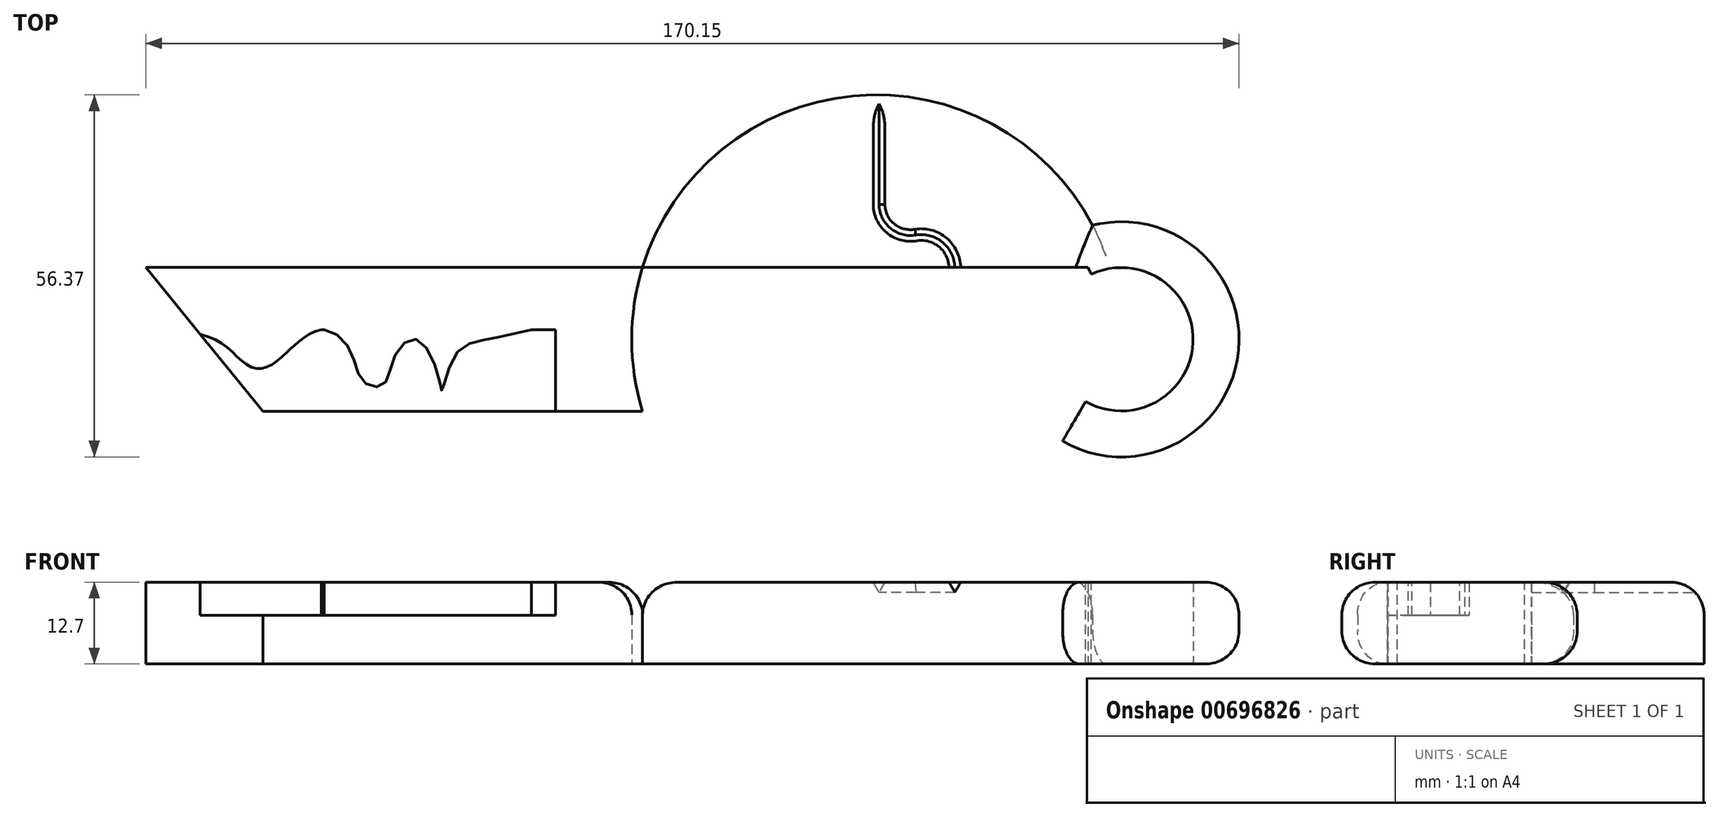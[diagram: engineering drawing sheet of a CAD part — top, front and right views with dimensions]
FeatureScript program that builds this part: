
annotation { "Feature Type Name" : "Feature", "Feature Type Description" : "" }
export const myFeature = defineFeature(function(context is Context, id is Id, definition is map)
    precondition{}
    {
        {
            var Q0;
            Q0=qCreatedBy(makeId("Top.planeOp"),FACE);
            var sketch = newSketch(context, id + "F0", { "sketchPlane" : qUnion([Q0])});
            skLineSegment(sketch, "E0", {"start": v(-76.55, 0) * mm, "end": v(76.12, 0) * mm});
            skLineSegment(sketch, "E1", {"start": v(0, 77.38) * mm, "end": v(0, -75.9) * mm});
            skLineSegment(sketch, "E2", {"start": v(0, 0) * mm, "end": v(76.12, 0) * mm});
            skLineSegment(sketch, "E3", {"start": v(38.06, 0) * mm, "end": v(38.06, 75.69) * mm});
            skCircle(sketch, "E4", {"center": v(38.06, 0) * mm, "radius": 38.06 * mm});
            skLineSegment(sketch, "E5.bottom", {"start": v(-75.64, 11.2) * mm, "end": v(74.43, 11.2) * mm});
            skLineSegment(sketch, "E5.top", {"start": v(-75.64, -11.2) * mm, "end": v(1.69, -11.2) * mm});
            skLineSegment(sketch, "E5.left", {"start": v(-75.64, 11.2) * mm, "end": v(-75.64, -11.2) * mm});
            skPoint(sketch, "E5.middle", {"position": v(0, 0) * mm});
            skSolve(sketch);
        }
        {
            var Q0;
            {var subQ0=sQuery(id+"F0.wireOp",EDGE,"E4");var subQ1=sQuery(id+"F0.wireOp",EDGE,"E3");var subQ2=makeQuery(id+"F0.imprint","INTERSECT",VERTEX,{"derivedFrom":[subQ1,subQ0]});Q0=makeQuery(id+"F0.imprint","IMPRINT",FACE,{"disambiguationData":[TD([[makeQuery(id+"F0.imprint","IMPRINT",EDGE,{"disambiguationData":[TD([[subQ2,1.0]])],"derivedFrom":subQ1}),1.0]])]});}
            var Q1;
            {var subQ0=sQuery(id+"F0.wireOp",EDGE,"E4");var subQ1=sQuery(id+"F0.wireOp",EDGE,"E3");var subQ2=makeQuery(id+"F0.imprint","INTERSECT",VERTEX,{"derivedFrom":[subQ1,subQ0]});Q1=makeQuery(id+"F0.imprint","IMPRINT",FACE,{"disambiguationData":[TD([[makeQuery(id+"F0.imprint","IMPRINT",EDGE,{"disambiguationData":[TD([[subQ2,1.0]])],"derivedFrom":subQ1}),-1.0]])]});}
            var Q2;
            {var subQ0=sQuery(id+"F0.wireOp",EDGE,"E4");var subQ1=sQuery(id+"F0.wireOp",EDGE,"E2");var subQ2=makeQuery(id+"F0.imprint","INTERSECT",VERTEX,{"derivedFrom":[subQ1,subQ0]});Q2=makeQuery(id+"F0.imprint","IMPRINT",FACE,{"disambiguationData":[TD([[makeQuery(id+"F0.imprint","IMPRINT",EDGE,{"disambiguationData":[TD([[subQ2,1.0]])],"derivedFrom":subQ1}),1.0]])]});}
            var Q3;
            {var subQ1=sQuery(id+"F0.wireOp",EDGE,"E2");var subQ3=sQuery(id+"F0.wireOp",EDGE,"E3");var subQ4=makeQuery(id+"F0.imprint","INTERSECT",VERTEX,{"derivedFrom":[subQ1,subQ3]});Q3=makeQuery(id+"F0.imprint","IMPRINT",FACE,{"disambiguationData":[TD([[makeQuery(id+"F0.imprint","IMPRINT",EDGE,{"disambiguationData":[TD([[subQ4,-1.0]])],"derivedFrom":subQ3}),1.0]])]});}
            var Q4;
            {var subQ0=sQuery(id+"F0.wireOp",EDGE,"E4");var subQ1=sQuery(id+"F0.wireOp",EDGE,"E2");var subQ4=makeQuery(id+"F0.imprint","INTERSECT",VERTEX,{"derivedFrom":[subQ1,subQ0]});Q4=makeQuery(id+"F0.imprint","IMPRINT",FACE,{"disambiguationData":[TD([[makeQuery(id+"F0.imprint","IMPRINT",EDGE,{"disambiguationData":[TD([[subQ4,1.0]])],"derivedFrom":subQ1}),-1.0]])]});}
            var Q5;
            {var subQ3=sQuery(id+"F0.wireOp",EDGE,"E5.left");var subQ5=sQuery(id+"F0.wireOp",EDGE,"E5.top");var subQ6=makeQuery(id+"F0.imprint","INTERSECT",VERTEX,{"derivedFrom":[subQ5,subQ3]});Q5=makeQuery(id+"F0.imprint","IMPRINT",FACE,{"disambiguationData":[TD([[makeQuery(id+"F0.imprint","IMPRINT",EDGE,{"disambiguationData":[TD([[subQ6,-1.0]])],"derivedFrom":subQ5}),1.0]])]});}
            var Q6;
            {var subQ3=sQuery(id+"F0.wireOp",EDGE,"E5.left");var subQ5=sQuery(id+"F0.wireOp",EDGE,"E5.bottom");var subQ7=makeQuery(id+"F0.imprint","INTERSECT",VERTEX,{"derivedFrom":[subQ5,subQ3]});Q6=makeQuery(id+"F0.imprint","IMPRINT",FACE,{"disambiguationData":[TD([[makeQuery(id+"F0.imprint","IMPRINT",EDGE,{"disambiguationData":[TD([[subQ7,-1.0]])],"derivedFrom":subQ5}),-1.0]])]});}
            var Q7;
            {var subQ1=sQuery(id+"F0.wireOp",EDGE,"E1");var subQ3=sQuery(id+"F0.wireOp",EDGE,"E5.bottom");var subQ4=makeQuery(id+"F0.imprint","INTERSECT",VERTEX,{"derivedFrom":[subQ1,subQ3]});Q7=makeQuery(id+"F0.imprint","IMPRINT",FACE,{"disambiguationData":[TD([[makeQuery(id+"F0.imprint","IMPRINT",EDGE,{"disambiguationData":[TD([[subQ4,-1.0]])],"derivedFrom":subQ3}),-1.0]])]});}
            var Q8;
            {var subQ0=sQuery(id+"F0.wireOp",EDGE,"E4");var subQ3=sQuery(id+"F0.wireOp",EDGE,"E5.top");var subQ5=makeQuery(id+"F0.imprint","INTERSECT",VERTEX,{"derivedFrom":[subQ0,subQ3]});Q8=makeQuery(id+"F0.imprint","IMPRINT",FACE,{"disambiguationData":[TD([[makeQuery(id+"F0.imprint","IMPRINT",EDGE,{"disambiguationData":[TD([[subQ5,1.0]])],"derivedFrom":subQ3}),1.0]])]});}
            extrude(context, id + "F1", {"entities" : qUnion([Q0, Q1, Q2, Q3, Q4, Q5, Q6, Q7, Q8]), "depth" : 12.7 * mm, "offsetDistance" : 25.4 * mm});
        }
        {
            var Q0;
            Q0=makeQuery(id+"F1.opExtrude","SWEPT_FACE",FACE,{"disambiguationData":[OSD([sQuery(id+"F0.wireOp",EDGE,"E5.top")])]});
            var sketch = newSketch(context, id + "F2", { "sketchPlane" : qUnion([Q0])});
            skPoint(sketch, "E6.oppositeSnap0", {"position": v(1.69, 6.35) * mm});
            skLineSegment(sketch, "E7.bottom", {"start": v(-75.64, 12.7) * mm, "end": v(-11.84, 12.7) * mm});
            skLineSegment(sketch, "E7.top", {"start": v(-75.64, 7.53) * mm, "end": v(-11.84, 7.53) * mm});
            skLineSegment(sketch, "E7.left", {"start": v(-75.64, 12.7) * mm, "end": v(-75.64, 7.53) * mm});
            skLineSegment(sketch, "E7.right", {"start": v(-11.84, 12.7) * mm, "end": v(-11.84, 7.53) * mm});
            skSolve(sketch);
        }
        {
            var Q0;
            Q0=qSketchRegion(id+"F2",true);
            extrude(context, id + "F3", {"entities" : qUnion([Q0]), "operationType" : NewBodyOperationType.REMOVE, "oppositeDirection" : true, "depth" : 12.7 * mm, "offsetDistance" : 25.4 * mm});
        }
        {
            var Q0;
            Q0=makeQuery(id+"F3.boolean.opBoolean","COPY",FACE,{"derivedFrom":makeQuery(id+"F3.opExtrude","SWEPT_FACE",FACE,{"disambiguationData":[OSD([sQuery(id+"F2.wireOp",EDGE,"E7.top")])]})});
            var sketch = newSketch(context, id + "F4", { "sketchPlane" : qUnion([Q0])});
            skPoint(sketch, "E8.8.internal.snap0", {"position": v(-43.74, 1.5) * mm});
            skFitSpline(sketch, "E8", {"points": [v(-71.4, 1.5) * mm, v(-64.86, 0) * mm, v(-61.37, -2.73) * mm, v(-58.75, -4.47) * mm, v(-56.14, -4.03) * mm, v(-53.52, -1.85) * mm, v(-51.34, 0) * mm, v(-47.85, 1.5) * mm, v(-43.74, -1.85) * mm, v(-41.75, -6.65) * mm, v(-38.7, -7.09) * mm, v(-36.95, -2.73) * mm, v(-33.46, 0) * mm, v(-29.98, -6.21) * mm, v(-29.54, -7.96) * mm, v(-27.36, -2.29) * mm, v(-22.56, 0) * mm, v(-15.59, 1.5) * mm], "startDerivative": vector(98.42, -12.85) * mm, "endDerivative": vector(95.91, 21.9) * mm});
            skLineSegment(sketch, "E9", {"start": v(-71.4, 1.5) * mm, "end": v(-15.59, 1.5) * mm});
            skSolve(sketch);
        }
        {
            var Q0;
            {var subQ0=sQuery(id+"F4.wireOp",EDGE,"E9");var subQ1=sQuery(id+"F4.wireOp",EDGE,"E8");var subQ3=makeQuery(id+"F4.imprint","INTERSECT",VERTEX,{"disambiguationData":[OD(0.0)],"derivedFrom":[subQ1,subQ0]});Q0=makeQuery(id+"F4.imprint","IMPRINT",FACE,{"disambiguationData":[TD([[makeQuery(id+"F4.imprint","IMPRINT",EDGE,{"disambiguationData":[TD([[subQ3,1.0]])],"derivedFrom":subQ1}),1.0]])]});}
            var Q1;
            {var subQ0=sQuery(id+"F4.wireOp",EDGE,"E9");var subQ1=sQuery(id+"F4.wireOp",EDGE,"E8");var subQ3=makeQuery(id+"F4.imprint","INTERSECT",VERTEX,{"disambiguationData":[OD(1.0)],"derivedFrom":[subQ1,subQ0]});Q1=makeQuery(id+"F4.imprint","IMPRINT",FACE,{"disambiguationData":[TD([[makeQuery(id+"F4.imprint","IMPRINT",EDGE,{"disambiguationData":[TD([[subQ3,-1.0]])],"derivedFrom":subQ1}),1.0]])]});}
            var Q2;
            Q2=makeQuery(id+"F1.opExtrude","CAP_FACE",FACE,{"disambiguationData":[OSD([sQuery(id+"F0.wireOp",EDGE,"E4"),sQuery(id+"F0.wireOp",EDGE,"E5.bottom"),sQuery(id+"F0.wireOp",EDGE,"E5.top"),sQuery(id+"F0.wireOp",EDGE,"E5.left")])],"isStart":false});
            extrude(context, id + "F5", {"entities" : qUnion([Q0, Q1]), "operationType" : NewBodyOperationType.ADD, "endBound" : BoundingType.UP_TO_SURFACE, "depth" : 25.4 * mm, "endBoundEntityFace" : qUnion([Q2]), "offsetDistance" : 25.4 * mm});
        }
        {
            var Q0;
            {var subQ0=sQuery(id+"F0.wireOp",EDGE,"E5.left");var subQ1=sQuery(id+"F0.wireOp",EDGE,"E5.top");var subQ2=sQuery(id+"F0.wireOp",EDGE,"E5.bottom");var subQ3=sQuery(id+"F0.wireOp",EDGE,"E4");Q0=makeQuery(id+"F5.boolean.opBoolean","MERGE",FACE,{"derivedFrom":[makeQuery(id+"F1.opExtrude","CAP_FACE",FACE,{"disambiguationData":[OSD([subQ3,subQ2,subQ1,subQ0])],"isStart":false}),makeQuery(id+"F5.opExtrude","CAP_FACE",FACE,{"disambiguationData":[OSD([subQ3,subQ2,subQ1,subQ0]),OD(0.0)],"isStart":false}),makeQuery(id+"F5.opExtrude","CAP_FACE",FACE,{"disambiguationData":[OSD([subQ3,subQ2,subQ1,subQ0]),OD(1.0)],"isStart":false})]});}
            var sketch = newSketch(context, id + "F6", { "sketchPlane" : qUnion([Q0])});
            skLineSegment(sketch, "E10", {"start": v(-54.4, -14.93) * mm, "end": v(-80.56, -12.75) * mm});
            skLineSegment(sketch, "E11", {"start": v(-80.56, -12.75) * mm, "end": v(-75.64, 11.2) * mm});
            skLineSegment(sketch, "E12", {"start": v(-75.64, 11.2) * mm, "end": v(-54.4, -14.93) * mm});
            skSolve(sketch);
        }
        {
            var Q0;
            Q0=qSketchRegion(id+"F6",true);
            extrude(context, id + "F7", {"entities" : qUnion([Q0]), "operationType" : NewBodyOperationType.REMOVE, "endBound" : BoundingType.THROUGH_ALL, "oppositeDirection" : true, "depth" : 25.4 * mm, "offsetDistance" : 25.4 * mm});
        }
        {
            var Q0;
            Q0=qCreatedBy(makeId("Right.planeOp"),FACE);
            cPlane(context, id + "F8", {"entities" : qUnion([Q0]), "cplaneType" : CPlaneType.OFFSET, "offset" : 76.2 * mm, "width" : 152.4 * mm, "height" : 152.4 * mm});
        }
        {
            var Q0;
            Q0=qCreatedBy(id+"F8.planeOp",FACE);
            var sketch = newSketch(context, id + "F9", { "sketchPlane" : qUnion([Q0])});
            skLineSegment(sketch, "E13", {"start": v(0, -5.67) * mm, "end": v(0, 19.48) * mm});
            skLineSegment(sketch, "E14.top", {"start": v(11.16, 0) * mm, "end": v(18.3, 0) * mm});
            skLineSegment(sketch, "E15", {"start": v(11.16, 0) * mm, "end": v(11.16, 12.7) * mm});
            skLineSegment(sketch, "E16", {"start": v(11.16, 12.7) * mm, "end": v(18.3, 12.7) * mm});
            skLineSegment(sketch, "E17", {"start": v(18.3, 12.7) * mm, "end": v(18.3, 0) * mm});
            skSolve(sketch);
        }
        {
            var Q0;
            Q0=makeQuery(id+"F9.imprint","IMPRINT",FACE,{"disambiguationData":[TD([[makeQuery(id+"F9.imprint","IMPRINT",EDGE,{"derivedFrom":sQuery(id+"F9.wireOp",EDGE,"E14.top")}),1.0]])]});
            var Q1;
            Q1=sQuery(id+"F9.wireOp",EDGE,"E13");
            revolve(context, id + "F10", {"operationType" : NewBodyOperationType.ADD, "entities" : qUnion([Q0]), "axis" : qUnion([Q1]), "revolveType" : RevolveType.TWO_DIRECTIONS, "angle" : 25 * degree, "angleBack" : 150 * degree});
        }
        {
            var Q0;
            Q0=qCreatedBy(makeId("Front.planeOp"),FACE);
            cPlane(context, id + "F11", {"entities" : qUnion([Q0]), "cplaneType" : CPlaneType.OFFSET, "offset" : 38.1 * mm, "width" : 152.4 * mm, "height" : 152.4 * mm});
        }
        {
            var Q0;
            {var subQ0=sQuery(id+"F0.wireOp",EDGE,"E5.left");var subQ1=sQuery(id+"F0.wireOp",EDGE,"E5.top");var subQ2=sQuery(id+"F0.wireOp",EDGE,"E5.bottom");var subQ3=sQuery(id+"F0.wireOp",EDGE,"E4");Q0=makeQuery(id+"F5.boolean.opBoolean","MERGE",FACE,{"derivedFrom":[makeQuery(id+"F1.opExtrude","CAP_FACE",FACE,{"disambiguationData":[OSD([subQ3,subQ2,subQ1,subQ0])],"isStart":false}),makeQuery(id+"F5.opExtrude","CAP_FACE",FACE,{"disambiguationData":[OSD([subQ3,subQ2,subQ1,subQ0]),OD(0.0)],"isStart":false}),makeQuery(id+"F5.opExtrude","CAP_FACE",FACE,{"disambiguationData":[OSD([subQ3,subQ2,subQ1,subQ0]),OD(1.0)],"isStart":false})]});}
            var sketch = newSketch(context, id + "F12", { "sketchPlane" : qUnion([Q0])});
            skLineSegment(sketch, "E18", {"start": v(38.5, -38.06) * mm, "end": v(38.5, -21.04) * mm});
            skArc(sketch, "E19", {"start": v(38.5, -21.04) * mm, "mid": v(40.22, -17.32) * mm, "end": v(44.17, -16.24) * mm});
            skArc(sketch, "E20", {"start": v(44.17, -16.24) * mm, "mid": v(48.62, -14.91) * mm, "end": v(50.28, -10.57) * mm});
            skLineSegment(sketch, "E21", {"start": v(50.28, -10.57) * mm, "end": v(50.28, 0) * mm});
            skLineSegment(sketch, "E22", {"start": v(0, 0) * mm, "end": v(43.3, 0) * mm});
            skLineSegment(sketch, "E23.MirrorCS", {"start": v(50.28, 10.57) * mm, "end": v(50.28, 0) * mm});
            skArc(sketch, "E24.MirrorCS", {"start": v(44.17, 16.24) * mm, "mid": v(48.62, 14.91) * mm, "end": v(50.28, 10.57) * mm});
            skArc(sketch, "E25.MirrorCS", {"start": v(38.5, 21.04) * mm, "mid": v(40.22, 17.32) * mm, "end": v(44.17, 16.24) * mm});
            skLineSegment(sketch, "E26.MirrorCS", {"start": v(38.5, 38.06) * mm, "end": v(38.5, 21.04) * mm});
            skSolve(sketch);
        }
        {
            var Q0;
            Q0=qCreatedBy(id+"F11.planeOp",FACE);
            var sketch = newSketch(context, id + "F13", { "sketchPlane" : qUnion([Q0])});
            skCircle(sketch, "E27.cCircle", {"center": v(38.5, 12.73) * mm, "radius": 1.6 * mm, "construction": true});
            skLineSegment(sketch, "E27.0", {"start": v(38.5, 11.14) * mm, "end": v(37.1, 13.53) * mm});
            skLineSegment(sketch, "E27.1", {"start": v(37.1, 13.53) * mm, "end": v(39.87, 13.53) * mm});
            skLineSegment(sketch, "E27.2", {"start": v(39.87, 13.53) * mm, "end": v(38.5, 11.14) * mm});
            skSolve(sketch);
        }
        {
            var Q0;
            Q0=makeQuery(id+"F13.imprint","IMPRINT",FACE,{"disambiguationData":[TD([[makeQuery(id+"F13.imprint","IMPRINT",EDGE,{"derivedFrom":sQuery(id+"F13.wireOp",EDGE,"E27.0")}),-1.0]])]});
            var Q1;
            Q1=sQuery(id+"F12.wireOp",EDGE,"E18");
            var Q2;
            Q2=sQuery(id+"F12.wireOp",EDGE,"E19");
            var Q3;
            Q3=sQuery(id+"F12.wireOp",EDGE,"E20");
            var Q4;
            Q4=sQuery(id+"F12.wireOp",EDGE,"E21");
            var Q5;
            Q5=sQuery(id+"F12.wireOp",EDGE,"E23.MirrorCS");
            var Q6;
            Q6=sQuery(id+"F12.wireOp",EDGE,"E24.MirrorCS");
            var Q7;
            Q7=sQuery(id+"F12.wireOp",EDGE,"E25.MirrorCS");
            var Q8;
            Q8=sQuery(id+"F12.wireOp",EDGE,"E26.MirrorCS");
            sweep(context, id + "F14", {"operationType" : NewBodyOperationType.REMOVE, "profiles" : qUnion([Q0]), "path" : qUnion([Q1, Q2, Q3, Q4, Q5, Q6, Q7, Q8])});
        }
        {
            var Q0;
            {var subQ0=sQuery(id+"F0.wireOp",EDGE,"E5.left");var subQ1=sQuery(id+"F0.wireOp",EDGE,"E5.top");var subQ2=sQuery(id+"F0.wireOp",EDGE,"E5.bottom");var subQ3=sQuery(id+"F0.wireOp",EDGE,"E4");var subQ4=makeQuery(id+"F5.opExtrude","CAP_FACE",FACE,{"disambiguationData":[OSD([subQ3,subQ2,subQ1,subQ0]),OD(0.0)],"isStart":false});var subQ5=makeQuery(id+"F1.opExtrude","SWEPT_FACE",FACE,{"disambiguationData":[OSD([subQ1])]});var subQ6=makeQuery(id+"F1.opExtrude","CAP_FACE",FACE,{"disambiguationData":[OSD([subQ3,subQ2,subQ1,subQ0])],"isStart":false});var subQ7=makeQuery(id+"F5.opExtrude","CAP_FACE",FACE,{"disambiguationData":[OSD([subQ3,subQ2,subQ1,subQ0]),OD(1.0)],"isStart":false});var subQ8=makeQuery(id+"F1.opExtrude","SWEPT_FACE",FACE,{"disambiguationData":[OSD([subQ3])]});Q0=makeQuery(id+"F14.boolean.opBoolean","SPLIT",EDGE,{"disambiguationData":[TD([subQ5])],"derivedFrom":makeQuery(id+"F10.boolean.opBoolean","SPLIT",EDGE,{"disambiguationData":[topologyDisambiguationEdgeConnected([subQ8,subQ6,subQ4,subQ7]),TD([subQ5])],"derivedFrom":makeQuery(id+"F1.opExtrude","CAP_EDGE",EDGE,{"disambiguationData":[OSD([subQ3])],"isStart":false})})});}
            var Q1;
            {var subQ0=sQuery(id+"F0.wireOp",EDGE,"E5.left");var subQ1=sQuery(id+"F0.wireOp",EDGE,"E5.top");var subQ2=sQuery(id+"F0.wireOp",EDGE,"E5.bottom");var subQ3=sQuery(id+"F0.wireOp",EDGE,"E4");var subQ4=makeQuery(id+"F5.opExtrude","CAP_FACE",FACE,{"disambiguationData":[OSD([subQ3,subQ2,subQ1,subQ0]),OD(1.0)],"isStart":false});var subQ5=makeQuery(id+"F1.opExtrude","CAP_FACE",FACE,{"disambiguationData":[OSD([subQ3,subQ2,subQ1,subQ0])],"isStart":false});var subQ6=makeQuery(id+"F10.opRevolve","SWEPT_FACE",FACE,{"disambiguationData":[OSD([sQuery(id+"F9.wireOp",EDGE,"E16")])]});var subQ7=makeQuery(id+"F5.opExtrude","CAP_FACE",FACE,{"disambiguationData":[OSD([subQ3,subQ2,subQ1,subQ0]),OD(0.0)],"isStart":false});var subQ8=makeQuery(id+"F1.opExtrude","SWEPT_FACE",FACE,{"disambiguationData":[OSD([subQ3])]});Q1=makeQuery(id+"F14.boolean.opBoolean","SPLIT",EDGE,{"disambiguationData":[TD([subQ6])],"derivedFrom":makeQuery(id+"F10.boolean.opBoolean","SPLIT",EDGE,{"disambiguationData":[topologyDisambiguationEdgeConnected([subQ8,subQ5,subQ7,subQ4]),TD([makeQuery(id+"F1.opExtrude","SWEPT_FACE",FACE,{"disambiguationData":[OSD([subQ1])]})])],"derivedFrom":makeQuery(id+"F1.opExtrude","CAP_EDGE",EDGE,{"disambiguationData":[OSD([subQ3])],"isStart":false})})});}
            var Q2;
            {var subQ0=sQuery(id+"F0.wireOp",EDGE,"E5.left");var subQ1=sQuery(id+"F0.wireOp",EDGE,"E5.top");var subQ2=sQuery(id+"F0.wireOp",EDGE,"E5.bottom");var subQ3=sQuery(id+"F0.wireOp",EDGE,"E4");var subQ4=makeQuery(id+"F5.opExtrude","CAP_FACE",FACE,{"disambiguationData":[OSD([subQ3,subQ2,subQ1,subQ0]),OD(1.0)],"isStart":false});var subQ5=makeQuery(id+"F1.opExtrude","CAP_FACE",FACE,{"disambiguationData":[OSD([subQ3,subQ2,subQ1,subQ0])],"isStart":false});var subQ6=makeQuery(id+"F5.opExtrude","CAP_FACE",FACE,{"disambiguationData":[OSD([subQ3,subQ2,subQ1,subQ0]),OD(0.0)],"isStart":false});var subQ7=makeQuery(id+"F1.opExtrude","SWEPT_FACE",FACE,{"disambiguationData":[OSD([subQ3])]});Q2=makeQuery(id+"F10.boolean.opBoolean","SPLIT",EDGE,{"disambiguationData":[topologyDisambiguationEdgeConnected([subQ7,subQ5,subQ6,subQ4]),TD([makeQuery(id+"F10.opRevolve","SWEPT_FACE",FACE,{"disambiguationData":[OSD([sQuery(id+"F9.wireOp",EDGE,"E15")])]})])],"derivedFrom":makeQuery(id+"F1.opExtrude","CAP_EDGE",EDGE,{"disambiguationData":[OSD([subQ3])],"isStart":false})});}
            var Q3;
            {var subQ0=sQuery(id+"F0.wireOp",EDGE,"E5.left");var subQ1=sQuery(id+"F0.wireOp",EDGE,"E5.top");var subQ2=sQuery(id+"F0.wireOp",EDGE,"E5.bottom");var subQ3=sQuery(id+"F0.wireOp",EDGE,"E4");var subQ4=makeQuery(id+"F5.opExtrude","CAP_FACE",FACE,{"disambiguationData":[OSD([subQ3,subQ2,subQ1,subQ0]),OD(0.0)],"isStart":false});var subQ5=makeQuery(id+"F1.opExtrude","CAP_FACE",FACE,{"disambiguationData":[OSD([subQ3,subQ2,subQ1,subQ0])],"isStart":false});var subQ6=makeQuery(id+"F5.opExtrude","CAP_FACE",FACE,{"disambiguationData":[OSD([subQ3,subQ2,subQ1,subQ0]),OD(1.0)],"isStart":false});var subQ7=makeQuery(id+"F1.opExtrude","SWEPT_FACE",FACE,{"disambiguationData":[OSD([subQ3])]});Q3=makeQuery(id+"F10.boolean.opBoolean","SPLIT",EDGE,{"disambiguationData":[topologyDisambiguationEdgeConnected([subQ7,subQ5,subQ4,subQ6]),TD([makeQuery(id+"F1.opExtrude","SWEPT_FACE",FACE,{"disambiguationData":[OSD([subQ2])]})])],"derivedFrom":makeQuery(id+"F1.opExtrude","CAP_EDGE",EDGE,{"disambiguationData":[OSD([subQ3])],"isStart":false})});}
            var Q4;
            Q4=makeQuery(id+"F10.opRevolve","SWEPT_EDGE",EDGE,{"disambiguationData":[OSD([sQuery(id+"F9.wireOp",EDGE,"E16"),sQuery(id+"F9.wireOp",EDGE,"E17")])]});
            var Q5;
            Q5=makeQuery(id+"F10.opRevolve","SWEPT_EDGE",EDGE,{"disambiguationData":[OSD([sQuery(id+"F9.wireOp",EDGE,"E14.top"),sQuery(id+"F9.wireOp",EDGE,"E17")])]});
            fillet(context, id + "F15", {"entities" : qUnion([Q0, Q1, Q2, Q3, Q4, Q5]), "radius" : 5.08 * mm, "tangentPropagation" : true, "allowEdgeOverflow" : false});
        }
    });
